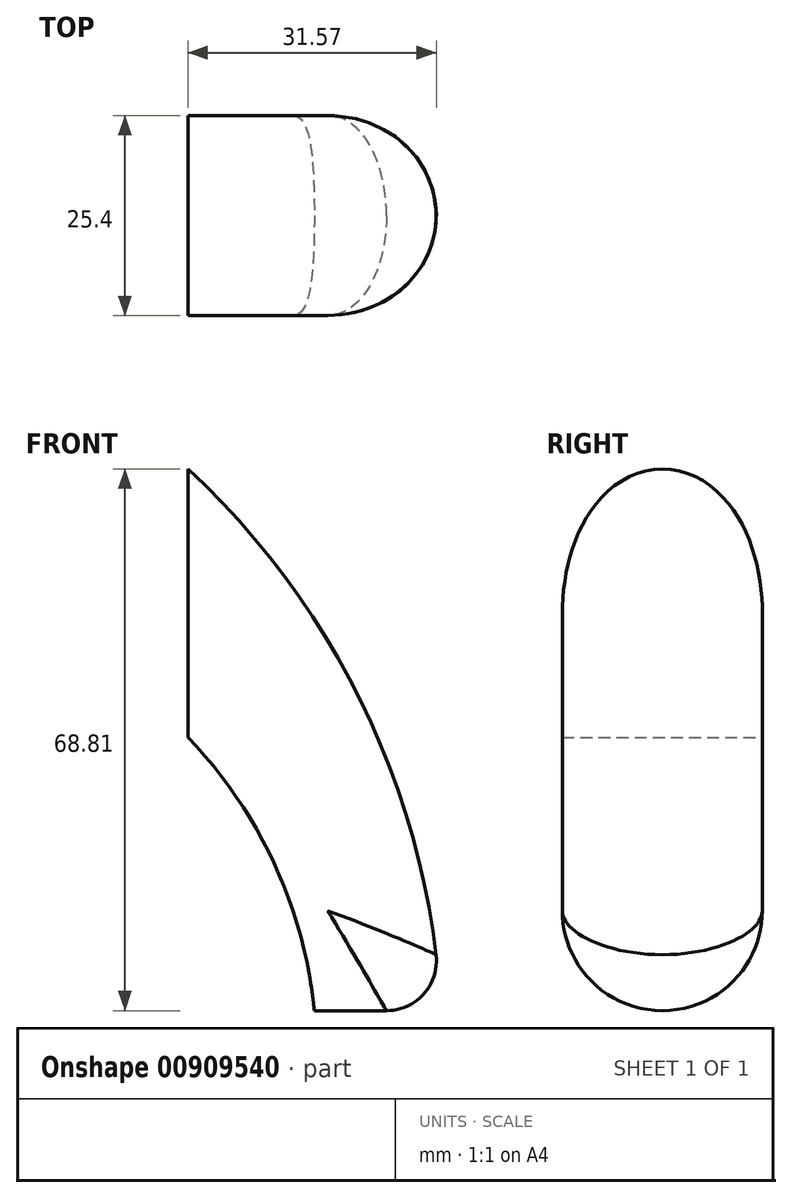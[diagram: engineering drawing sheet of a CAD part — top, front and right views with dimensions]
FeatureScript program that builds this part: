
annotation { "Feature Type Name" : "Feature", "Feature Type Description" : "" }
export const myFeature = defineFeature(function(context is Context, id is Id, definition is map)
    precondition{}
    {
        {
            var Q0;
            Q0=qCreatedBy(makeId("Front.planeOp"),FACE);
            var sketch = newSketch(context, id + "F0", { "sketchPlane" : qUnion([Q0])});
            skLineSegment(sketch, "E0", {"start": v(0, 34.08) * mm, "end": v(0, 0) * mm});
            skLineSegment(sketch, "E1", {"start": v(16.07, -34.73) * mm, "end": v(25.22, -34.73) * mm});
            skArc(sketch, "E2", {"start": v(31.52, -27.62) * mm, "mid": v(21.24, 6.03) * mm, "end": v(0, 34.08) * mm});
            skArc(sketch, "E3", {"start": v(16.07, -34.73) * mm, "mid": v(10.95, -16.02) * mm, "end": v(0, 0) * mm});
            skPoint(sketch, "E4.orphan", {"position": v(0, -34.73) * mm});
            skPoint(sketch, "E5.visualSharp", {"position": v(32.13, -34.73) * mm});
            skArc(sketch, "E5.filletArc", {"start": v(25.22, -34.73) * mm, "mid": v(29.97, -32.6) * mm, "end": v(31.52, -27.62) * mm});
            skSolve(sketch);
        }
        {
            var Q0;
            Q0=makeQuery(id+"F0.imprint","IMPRINT",FACE,{"disambiguationData":[TD([[makeQuery(id+"F0.imprint","IMPRINT",EDGE,{"derivedFrom":sQuery(id+"F0.wireOp",EDGE,"E0")}),1.0]])]});
            extrude(context, id + "F1", {"entities" : qUnion([Q0]), "depth" : 25.4 * mm, "offsetDistance" : 25.4 * mm});
        }
        {
            var Q0;
            Q0=makeQuery(id+"F1.opExtrude","CAP_EDGE",EDGE,{"disambiguationData":[OSD([sQuery(id+"F0.wireOp",EDGE,"E2")])],"isStart":false});
            var Q1;
            Q1=makeQuery(id+"F1.opExtrude","CAP_EDGE",EDGE,{"disambiguationData":[OSD([sQuery(id+"F0.wireOp",EDGE,"E2")])],"isStart":true});
            fillet(context, id + "F2", {"entities" : qUnion([Q0, Q1]), "radius" : 12.7 * mm, "tangentPropagation" : true, "allowEdgeOverflow" : false});
        }
    });
